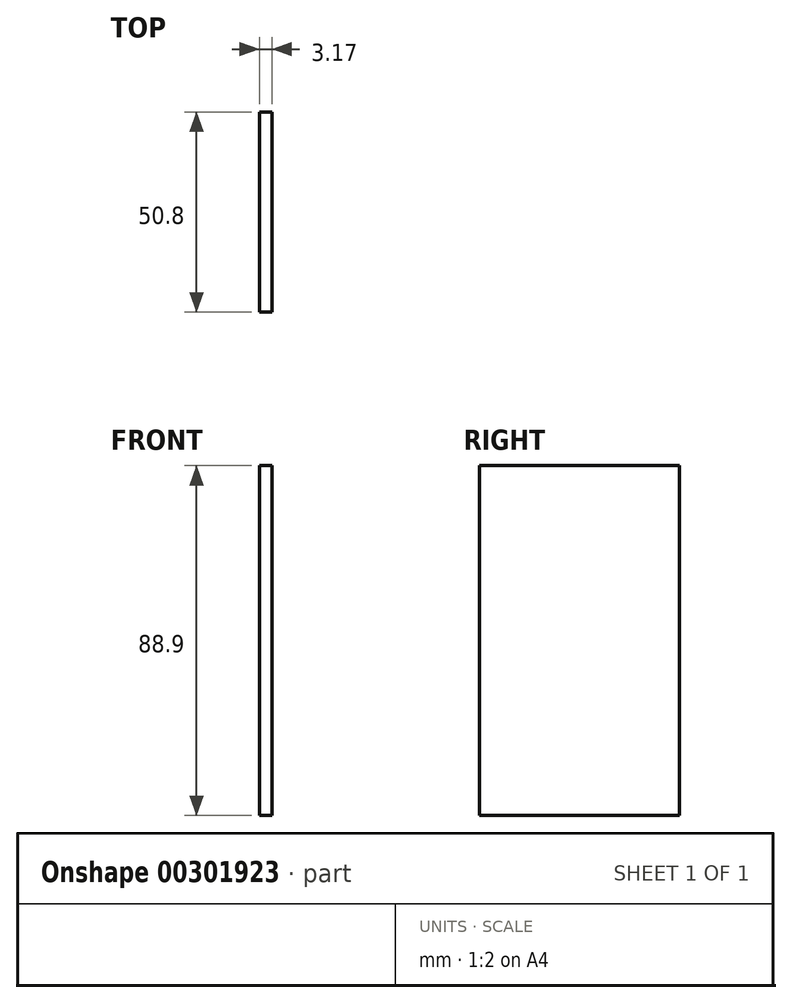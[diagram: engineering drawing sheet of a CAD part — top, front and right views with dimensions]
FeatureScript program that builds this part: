
annotation { "Feature Type Name" : "Feature", "Feature Type Description" : "" }
export const myFeature = defineFeature(function(context is Context, id is Id, definition is map)
    precondition{}
    {
        {
            var Q0;
            Q0=qCreatedBy(makeId("Right.planeOp"),FACE);
            var sketch = newSketch(context, id + "F0", { "sketchPlane" : qUnion([Q0])});
            skLineSegment(sketch, "E0.bottom", {"start": v(25.4, 44.45) * mm, "end": v(-25.4, 44.45) * mm});
            skLineSegment(sketch, "E0.top", {"start": v(25.4, -44.45) * mm, "end": v(-25.4, -44.45) * mm});
            skLineSegment(sketch, "E0.left", {"start": v(25.4, 44.45) * mm, "end": v(25.4, -44.45) * mm});
            skLineSegment(sketch, "E0.right", {"start": v(-25.4, 44.45) * mm, "end": v(-25.4, -44.45) * mm});
            skPoint(sketch, "E0.middle", {"position": v(0, 0) * mm});
            skSolve(sketch);
        }
        {
            var Q0;
            Q0=makeQuery(id+"F0.imprint","IMPRINT",FACE,{"disambiguationData":[TD([[makeQuery(id+"F0.imprint","IMPRINT",EDGE,{"derivedFrom":sQuery(id+"F0.wireOp",EDGE,"E0.bottom")}),1.0]])]});
            extrude(context, id + "F1", {"entities" : qUnion([Q0]), "depth" : 3.17 * mm});
        }
    });
